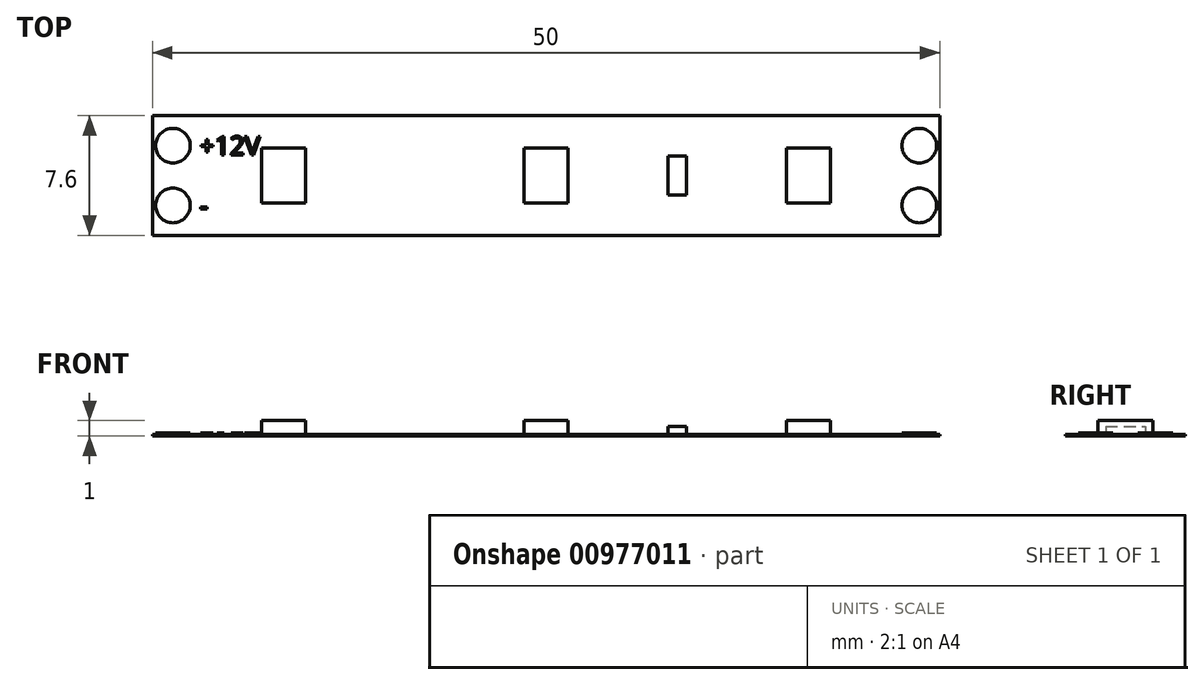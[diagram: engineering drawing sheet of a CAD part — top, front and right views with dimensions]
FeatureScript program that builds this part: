
annotation { "Feature Type Name" : "Feature", "Feature Type Description" : "" }
export const myFeature = defineFeature(function(context is Context, id is Id, definition is map)
    precondition{}
    {
        {
            var Q0;
            Q0=qCreatedBy(makeId("Top.planeOp"),FACE);
            var sketch = newSketch(context, id + "F0", { "sketchPlane" : qUnion([Q0])});
            skLineSegment(sketch, "E0.bottom", {"start": v(-25, 3.8) * mm, "end": v(25, 3.8) * mm});
            skLineSegment(sketch, "E0.top", {"start": v(-25, -3.8) * mm, "end": v(25, -3.8) * mm});
            skLineSegment(sketch, "E0.left", {"start": v(-25, 3.8) * mm, "end": v(-25, -3.8) * mm});
            skLineSegment(sketch, "E0.right", {"start": v(25, 3.8) * mm, "end": v(25, -3.8) * mm});
            skPoint(sketch, "E0.middle", {"position": v(0, 0) * mm});
            skLineSegment(sketch, "E1.bottom", {"start": v(-1.4, 1.75) * mm, "end": v(1.4, 1.75) * mm});
            skLineSegment(sketch, "E1.top", {"start": v(-1.4, -1.75) * mm, "end": v(1.4, -1.75) * mm});
            skLineSegment(sketch, "E1.left", {"start": v(-1.4, 1.75) * mm, "end": v(-1.4, -1.75) * mm});
            skLineSegment(sketch, "E1.right", {"start": v(1.4, 1.75) * mm, "end": v(1.4, -1.75) * mm});
            skLineSegment(sketch, "E2", {"start": v(-16.66, 7.03) * mm, "end": v(-16.66, -7.93) * mm, "construction": true});
            skLineSegment(sketch, "E3", {"start": v(16.66, 5.4) * mm, "end": v(16.66, -7.08) * mm, "construction": true});
            skLineSegment(sketch, "E4", {"start": v(-30.47, 0) * mm, "end": v(28.27, 0) * mm, "construction": true});
            skLineSegment(sketch, "E5.bottom", {"start": v(-18.06, 1.75) * mm, "end": v(-15.26, 1.75) * mm});
            skLineSegment(sketch, "E5.top", {"start": v(-18.06, -1.75) * mm, "end": v(-15.26, -1.75) * mm});
            skLineSegment(sketch, "E5.left", {"start": v(-18.06, 1.75) * mm, "end": v(-18.06, -1.75) * mm});
            skLineSegment(sketch, "E5.right", {"start": v(-15.26, 1.75) * mm, "end": v(-15.26, -1.75) * mm});
            skPoint(sketch, "E5.middle", {"position": v(-16.66, 0) * mm});
            skLineSegment(sketch, "E6.bottom", {"start": v(15.26, 1.75) * mm, "end": v(18.06, 1.75) * mm});
            skLineSegment(sketch, "E6.top", {"start": v(15.26, -1.75) * mm, "end": v(18.06, -1.75) * mm});
            skLineSegment(sketch, "E6.left", {"start": v(15.26, 1.75) * mm, "end": v(15.26, -1.75) * mm});
            skLineSegment(sketch, "E6.right", {"start": v(18.06, 1.75) * mm, "end": v(18.06, -1.75) * mm});
            skPoint(sketch, "E6.middle", {"position": v(16.66, 0) * mm});
            skLineSegment(sketch, "E7", {"start": v(8.33, 5.08) * mm, "end": v(8.33, -6.07) * mm, "construction": true});
            skLineSegment(sketch, "E8.bottom", {"start": v(8.93, -1.25) * mm, "end": v(7.73, -1.25) * mm});
            skLineSegment(sketch, "E8.top", {"start": v(8.93, 1.25) * mm, "end": v(7.73, 1.25) * mm});
            skLineSegment(sketch, "E8.left", {"start": v(8.93, -1.25) * mm, "end": v(8.93, 1.25) * mm});
            skLineSegment(sketch, "E8.right", {"start": v(7.73, -1.25) * mm, "end": v(7.73, 1.25) * mm});
            skPoint(sketch, "E8.middle", {"position": v(8.33, 0) * mm});
            skLineSegment(sketch, "E9", {"start": v(-26.86, 1.9) * mm, "end": v(27.27, 1.9) * mm, "construction": true});
            skLineSegment(sketch, "E10", {"start": v(-27.01, -1.9) * mm, "end": v(26.66, -1.9) * mm, "construction": true});
            skCircle(sketch, "E11", {"center": v(-23.7, 1.9) * mm, "radius": 1.1 * mm});
            skCircle(sketch, "E12", {"center": v(-23.7, -1.9) * mm, "radius": 1.1 * mm});
            skCircle(sketch, "E13", {"center": v(23.7, 1.9) * mm, "radius": 1.1 * mm});
            skCircle(sketch, "E14", {"center": v(23.7, -1.9) * mm, "radius": 1.1 * mm});
            skText(sketch, "E15", { "text": "+12V", "fontName": "OpenSans-Regular.ttf"});
            skText(sketch, "E16", { "text": "-", "fontName": "OpenSans-Regular.ttf"});
            const initialGuessF0  = {"E15": [-0.022, 0.0013, 1, 0, 0.0012], "E16": [-0.022, -0.0025, 1, 0, 0.0012]};
            skSetInitialGuess(sketch, initialGuessF0);
            skSolve(sketch);
        }
        {
            var Q0;
            Q0=makeQuery(id+"F0.imprint","IMPRINT",FACE,{"disambiguationData":[TD([[makeQuery(id+"F0.imprint","IMPRINT",EDGE,{"derivedFrom":sQuery(id+"F0.wireOp",EDGE,"E0.bottom")}),-1.0]])]});
            var Q1;
            Q1=makeQuery(id+"F0.imprint","IMPRINT",FACE,{"disambiguationData":[TD([[makeQuery(id+"F0.imprint","IMPRINT",EDGE,{"derivedFrom":sQuery(id+"F0.wireOp",EDGE,"E12")}),1.0]])]});
            var Q2;
            Q2=makeQuery(id+"F0.imprint","IMPRINT",FACE,{"disambiguationData":[TD([[makeQuery(id+"F0.imprint","IMPRINT",EDGE,{"derivedFrom":sQuery(id+"F0.wireOp",EDGE,"E5.bottom")}),-1.0]])]});
            var Q3;
            Q3=makeQuery(id+"F0.imprint","IMPRINT",FACE,{"disambiguationData":[TD([[makeQuery(id+"F0.imprint","IMPRINT",EDGE,{"derivedFrom":sQuery(id+"F0.wireOp",EDGE,"E11")}),1.0]])]});
            var Q4;
            Q4=makeQuery(id+"F0.imprint","IMPRINT",FACE,{"disambiguationData":[TD([[makeQuery(id+"F0.imprint","IMPRINT",EDGE,{"derivedFrom":sQuery(id+"F0.wireOp",EDGE,"E1.bottom")}),-1.0]])]});
            var Q5;
            Q5=makeQuery(id+"F0.imprint","IMPRINT",FACE,{"disambiguationData":[TD([[makeQuery(id+"F0.imprint","IMPRINT",EDGE,{"derivedFrom":sQuery(id+"F0.wireOp",EDGE,"E8.bottom")}),-1.0]])]});
            var Q6;
            Q6=makeQuery(id+"F0.imprint","IMPRINT",FACE,{"disambiguationData":[TD([[makeQuery(id+"F0.imprint","IMPRINT",EDGE,{"derivedFrom":sQuery(id+"F0.wireOp",EDGE,"E6.bottom")}),-1.0]])]});
            var Q7;
            Q7=makeQuery(id+"F0.imprint","IMPRINT",FACE,{"disambiguationData":[TD([[makeQuery(id+"F0.imprint","IMPRINT",EDGE,{"derivedFrom":sQuery(id+"F0.wireOp",EDGE,"E14")}),1.0]])]});
            var Q8;
            Q8=makeQuery(id+"F0.imprint","IMPRINT",FACE,{"disambiguationData":[TD([[makeQuery(id+"F0.imprint","IMPRINT",EDGE,{"derivedFrom":sQuery(id+"F0.wireOp",EDGE,"E13")}),1.0]])]});
            var Q9;
            Q9=makeQuery(id+"F0.imprint","IMPRINT",FACE,{"disambiguationData":[TD([[makeQuery(id+"F0.imprint","IMPRINT",EDGE,{"derivedFrom":sQuery(id+"F0.wireOp",EDGE,"E15.sketch_text.stroke-21")}),-1.0]])]});
            var Q10;
            Q10=makeQuery(id+"F0.imprint","IMPRINT",FACE,{"disambiguationData":[TD([[makeQuery(id+"F0.imprint","IMPRINT",EDGE,{"derivedFrom":sQuery(id+"F0.wireOp",EDGE,"E15.sketch_text.stroke-41")}),-1.0]])]});
            var Q11;
            Q11=makeQuery(id+"F0.imprint","IMPRINT",FACE,{"disambiguationData":[TD([[makeQuery(id+"F0.imprint","IMPRINT",EDGE,{"derivedFrom":sQuery(id+"F0.wireOp",EDGE,"E15.sketch_text.stroke-12")}),-1.0]])]});
            var Q12;
            Q12=makeQuery(id+"F0.imprint","IMPRINT",FACE,{"disambiguationData":[TD([[makeQuery(id+"F0.imprint","IMPRINT",EDGE,{"derivedFrom":sQuery(id+"F0.wireOp",EDGE,"E15.sketch_text.stroke-0")}),-1.0]])]});
            var Q13;
            Q13=makeQuery(id+"F0.imprint","IMPRINT",FACE,{"disambiguationData":[TD([[makeQuery(id+"F0.imprint","IMPRINT",EDGE,{"derivedFrom":sQuery(id+"F0.wireOp",EDGE,"E16.sketch_text.stroke-0")}),-1.0]])]});
            extrude(context, id + "F1", {"entities" : qUnion([Q0, Q1, Q2, Q3, Q4, Q5, Q6, Q7, Q8, Q9, Q10, Q11, Q12, Q13]), "oppositeDirection" : true, "depth" : 0.1 * mm, "offsetDistance" : 25 * mm});
        }
        {
            var Q0;
            Q0=makeQuery(id+"F0.imprint","IMPRINT",FACE,{"disambiguationData":[TD([[makeQuery(id+"F0.imprint","IMPRINT",EDGE,{"derivedFrom":sQuery(id+"F0.wireOp",EDGE,"E5.bottom")}),-1.0]])]});
            extrude(context, id + "F2", {"entities" : qUnion([Q0]), "depth" : 0.9 * mm, "offsetDistance" : 25 * mm});
        }
        {
            var Q0;
            Q0=makeQuery(id+"F0.imprint","IMPRINT",FACE,{"disambiguationData":[TD([[makeQuery(id+"F0.imprint","IMPRINT",EDGE,{"derivedFrom":sQuery(id+"F0.wireOp",EDGE,"E1.bottom")}),-1.0]])]});
            var Q1;
            Q1=makeQuery(id+"F0.imprint","IMPRINT",FACE,{"disambiguationData":[TD([[makeQuery(id+"F0.imprint","IMPRINT",EDGE,{"derivedFrom":sQuery(id+"F0.wireOp",EDGE,"E6.bottom")}),-1.0]])]});
            extrude(context, id + "F3", {"entities" : qUnion([Q0, Q1]), "operationType" : NewBodyOperationType.ADD, "depth" : 0.9 * mm, "offsetDistance" : 25 * mm});
        }
        {
            var Q0;
            Q0=makeQuery(id+"F0.imprint","IMPRINT",FACE,{"disambiguationData":[TD([[makeQuery(id+"F0.imprint","IMPRINT",EDGE,{"derivedFrom":sQuery(id+"F0.wireOp",EDGE,"E8.bottom")}),-1.0]])]});
            extrude(context, id + "F4", {"entities" : qUnion([Q0]), "operationType" : NewBodyOperationType.ADD, "depth" : 0.5 * mm, "offsetDistance" : 25 * mm});
        }
        {
            var Q0;
            Q0=makeQuery(id+"F0.imprint","IMPRINT",FACE,{"disambiguationData":[TD([[makeQuery(id+"F0.imprint","IMPRINT",EDGE,{"derivedFrom":sQuery(id+"F0.wireOp",EDGE,"E12")}),1.0]])]});
            var Q1;
            Q1=makeQuery(id+"F0.imprint","IMPRINT",FACE,{"disambiguationData":[TD([[makeQuery(id+"F0.imprint","IMPRINT",EDGE,{"derivedFrom":sQuery(id+"F0.wireOp",EDGE,"E11")}),1.0]])]});
            var Q2;
            Q2=makeQuery(id+"F0.imprint","IMPRINT",FACE,{"disambiguationData":[TD([[makeQuery(id+"F0.imprint","IMPRINT",EDGE,{"derivedFrom":sQuery(id+"F0.wireOp",EDGE,"E13")}),1.0]])]});
            var Q3;
            Q3=makeQuery(id+"F0.imprint","IMPRINT",FACE,{"disambiguationData":[TD([[makeQuery(id+"F0.imprint","IMPRINT",EDGE,{"derivedFrom":sQuery(id+"F0.wireOp",EDGE,"E14")}),1.0]])]});
            extrude(context, id + "F5", {"entities" : qUnion([Q0, Q1, Q2, Q3]), "operationType" : NewBodyOperationType.ADD, "depth" : 0.1 * mm, "offsetDistance" : 25 * mm});
        }
        {
            var Q0;
            Q0=makeQuery(id+"F0.imprint","IMPRINT",FACE,{"disambiguationData":[TD([[makeQuery(id+"F0.imprint","IMPRINT",EDGE,{"derivedFrom":sQuery(id+"F0.wireOp",EDGE,"E15.sketch_text.stroke-41")}),-1.0]])]});
            var Q1;
            Q1=makeQuery(id+"F0.imprint","IMPRINT",FACE,{"disambiguationData":[TD([[makeQuery(id+"F0.imprint","IMPRINT",EDGE,{"derivedFrom":sQuery(id+"F0.wireOp",EDGE,"E15.sketch_text.stroke-21")}),-1.0]])]});
            var Q2;
            Q2=makeQuery(id+"F0.imprint","IMPRINT",FACE,{"disambiguationData":[TD([[makeQuery(id+"F0.imprint","IMPRINT",EDGE,{"derivedFrom":sQuery(id+"F0.wireOp",EDGE,"E15.sketch_text.stroke-12")}),-1.0]])]});
            var Q3;
            Q3=makeQuery(id+"F0.imprint","IMPRINT",FACE,{"disambiguationData":[TD([[makeQuery(id+"F0.imprint","IMPRINT",EDGE,{"derivedFrom":sQuery(id+"F0.wireOp",EDGE,"E15.sketch_text.stroke-0")}),-1.0]])]});
            var Q4;
            Q4=makeQuery(id+"F0.imprint","IMPRINT",FACE,{"disambiguationData":[TD([[makeQuery(id+"F0.imprint","IMPRINT",EDGE,{"derivedFrom":sQuery(id+"F0.wireOp",EDGE,"E16.sketch_text.stroke-0")}),-1.0]])]});
            extrude(context, id + "F6", {"entities" : qUnion([Q0, Q1, Q2, Q3, Q4]), "operationType" : NewBodyOperationType.ADD, "depth" : 0.1 * mm, "offsetDistance" : 25 * mm});
        }
    });
